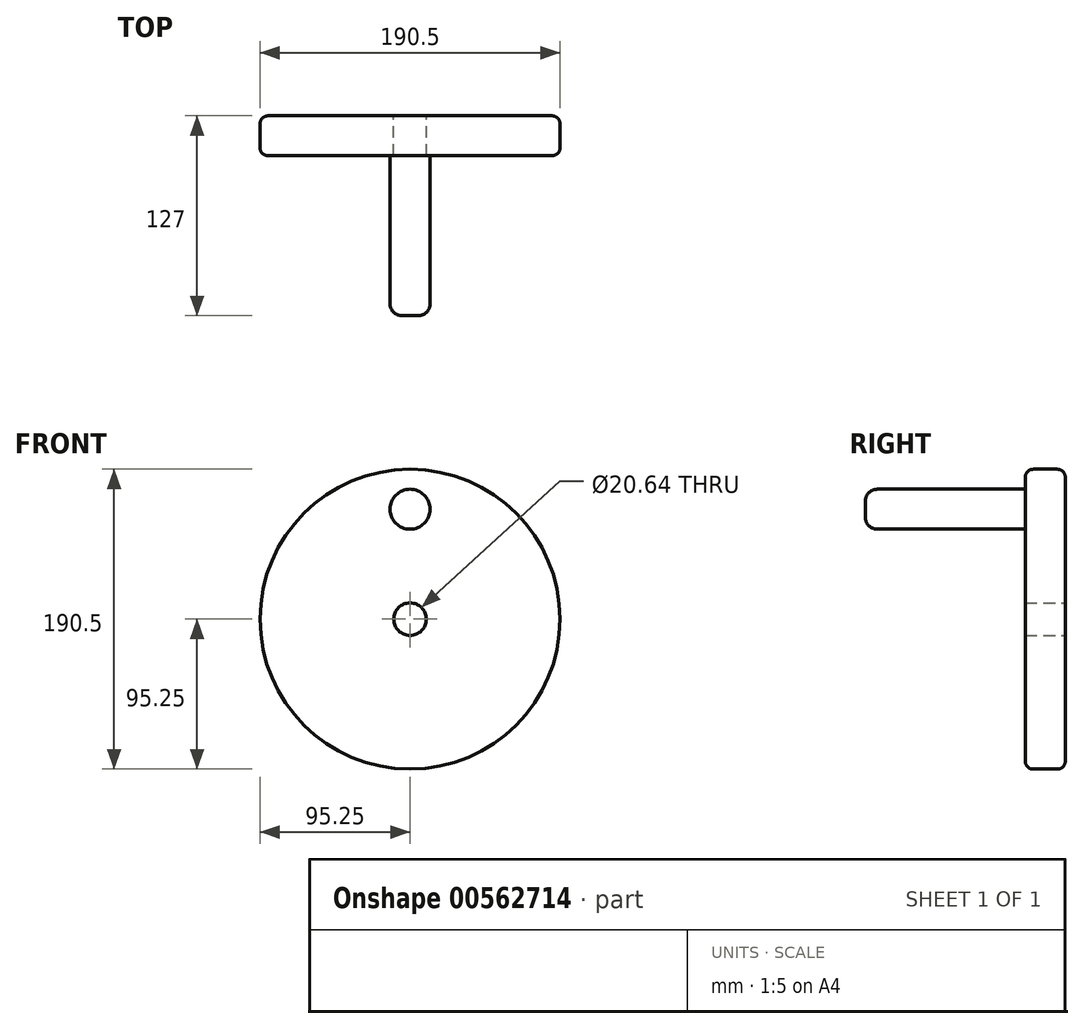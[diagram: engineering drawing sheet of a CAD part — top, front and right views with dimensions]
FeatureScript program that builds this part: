
annotation { "Feature Type Name" : "Feature", "Feature Type Description" : "" }
export const myFeature = defineFeature(function(context is Context, id is Id, definition is map)
    precondition{}
    {
        {
            var Q0;
            Q0=qCreatedBy(makeId("Front.planeOp"),FACE);
            var sketch = newSketch(context, id + "F0", { "sketchPlane" : qUnion([Q0])});
            skCircle(sketch, "E0", {"center": v(0, 0) * mm, "radius": 95.25 * mm});
            skPoint(sketch, "E1", {"position": v(0, 69.85) * mm});
            skCircle(sketch, "E2", {"center": v(0, 69.85) * mm, "radius": 12.7 * mm});
            skCircle(sketch, "E3", {"center": v(0, 0) * mm, "radius": 10.32 * mm});
            skSolve(sketch);
        }
        {
            var Q0;
            Q0=makeQuery(id+"F0.imprint","IMPRINT",FACE,{"disambiguationData":[TD([[makeQuery(id+"F0.imprint","IMPRINT",EDGE,{"derivedFrom":sQuery(id+"F0.wireOp",EDGE,"E0")}),1.0]])]});
            extrude(context, id + "F1", {"entities" : qUnion([Q0]), "depth" : 25.4 * mm, "offsetDistance" : 25.4 * mm});
        }
        {
            var Q0;
            Q0=makeQuery(id+"F0.imprint","IMPRINT",FACE,{"disambiguationData":[TD([[makeQuery(id+"F0.imprint","IMPRINT",EDGE,{"derivedFrom":sQuery(id+"F0.wireOp",EDGE,"E2")}),1.0]])]});
            extrude(context, id + "F2", {"entities" : qUnion([Q0]), "operationType" : NewBodyOperationType.ADD, "depth" : 127 * mm, "offsetDistance" : 25.4 * mm});
        }
        {
            var Q0;
            Q0=makeQuery(id+"F1.opExtrude","CAP_EDGE",EDGE,{"disambiguationData":[OSD([sQuery(id+"F0.wireOp",EDGE,"E0")])],"isStart":false});
            var Q1;
            Q1=makeQuery(id+"F1.opExtrude","CAP_EDGE",EDGE,{"disambiguationData":[OSD([sQuery(id+"F0.wireOp",EDGE,"E0")])],"isStart":true});
            fillet(context, id + "F3", {"entities" : qUnion([Q0, Q1]), "radius" : 5.08 * mm, "tangentPropagation" : true, "allowEdgeOverflow" : false});
        }
        {
            var Q0;
            Q0=makeQuery(id+"F2.opExtrude","CAP_EDGE",EDGE,{"disambiguationData":[OSD([sQuery(id+"F0.wireOp",EDGE,"E2")])],"isStart":false});
            fillet(context, id + "F4", {"entities" : qUnion([Q0]), "radius" : 7.62 * mm, "tangentPropagation" : true, "allowEdgeOverflow" : false});
        }
    });
